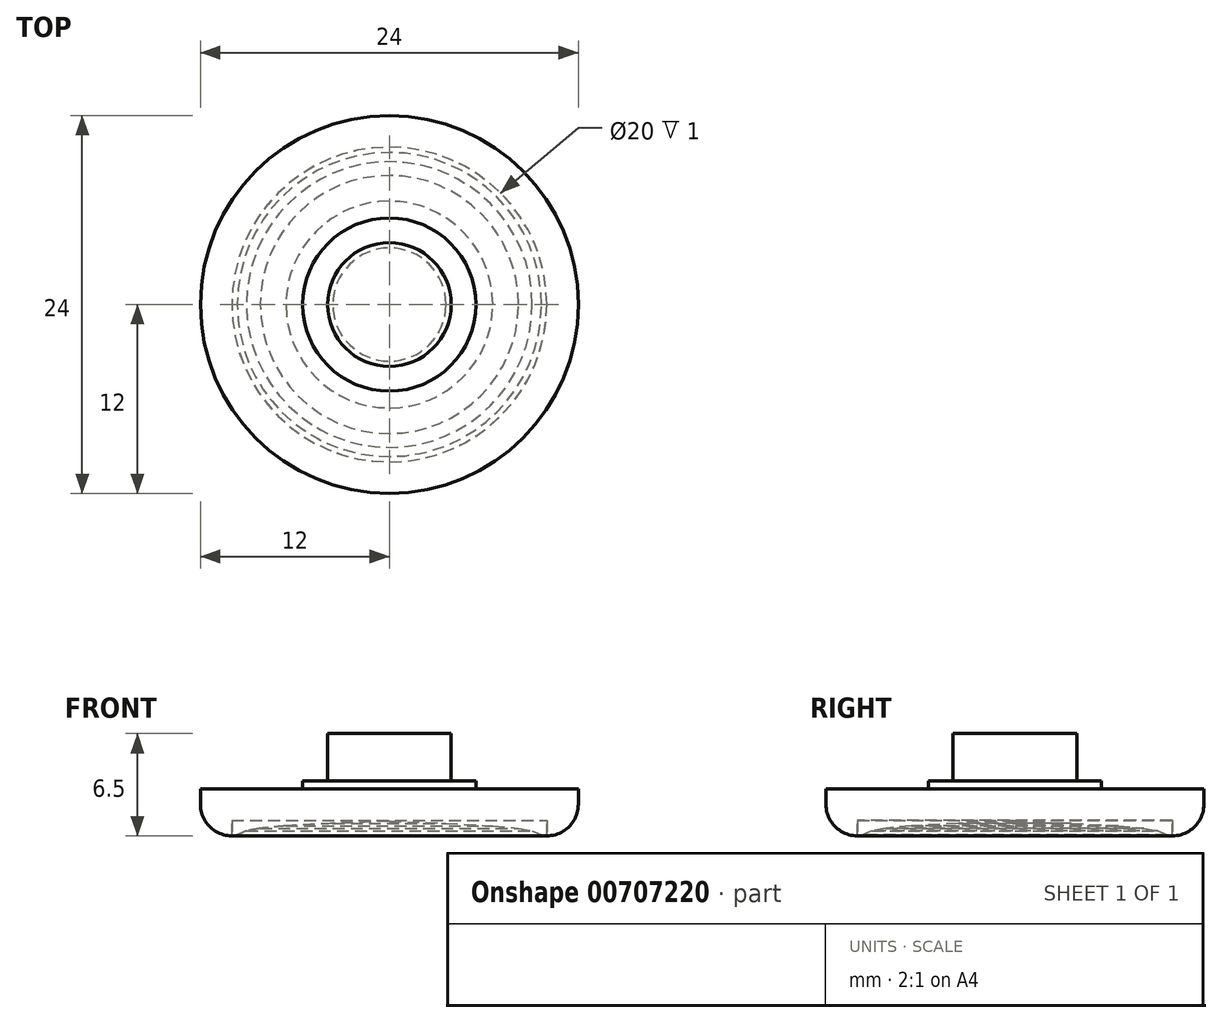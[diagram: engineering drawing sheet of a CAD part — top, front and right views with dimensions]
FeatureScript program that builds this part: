
annotation { "Feature Type Name" : "Feature", "Feature Type Description" : "" }
export const myFeature = defineFeature(function(context is Context, id is Id, definition is map)
    precondition{}
    {
        {
            var Q0;
            Q0=qCreatedBy(makeId("Top.planeOp"),FACE);
            var sketch = newSketch(context, id + "F0", { "sketchPlane" : qUnion([Q0])});
            skCircle(sketch, "E0", {"center": v(0, 0) * mm, "radius": 12 * mm});
            skSolve(sketch);
        }
        {
            var Q0;
            Q0 = qSketchRegion(id + "F0", true);
            extrude(context, id + "F1", {"entities" : qUnion([Q0]), "depth" : 2 * mm, "offsetDistance" : 25 * mm});
        }
        {
            var Q0;
            Q0=makeQuery(id+"F1.opExtrude","CAP_FACE",FACE,{"disambiguationData":[OSD([sQuery(id+"F0.wireOp",EDGE,"E0")])],"isStart":true});
            var sketch = newSketch(context, id + "F2", { "sketchPlane" : qUnion([Q0])});
            skCircle(sketch, "E1", {"center": v(0, 0) * mm, "radius": 10 * mm});
            skSolve(sketch);
        }
        {
            var Q0;
            Q0=makeQuery(id+"F2.imprint","IMPRINT",FACE,{"disambiguationData":[TD([[makeQuery(id+"F2.imprint","IMPRINT",EDGE,{"derivedFrom":sQuery(id+"F2.wireOp",EDGE,"E1")}),-1.0]])]});
            extrude(context, id + "F3", {"entities" : qUnion([Q0]), "operationType" : NewBodyOperationType.ADD, "depth" : 1 * mm, "offsetDistance" : 25 * mm});
        }
        {
            var Q0;
            Q0=makeQuery(id+"F3.opExtrude","CAP_EDGE",EDGE,{"disambiguationData":[OSD([sQuery(id+"F0.wireOp",EDGE,"E0")])],"isStart":false});
            fillet(context, id + "F4", {"entities" : qUnion([Q0]), "radius" : 2 * mm, "tangentPropagation" : true, "allowEdgeOverflow" : false});
        }
        {
            var Q0;
            Q0=makeQuery(id+"F1.opExtrude","CAP_FACE",FACE,{"disambiguationData":[OSD([sQuery(id+"F0.wireOp",EDGE,"E0")])],"isStart":false});
            var sketch = newSketch(context, id + "F5", { "sketchPlane" : qUnion([Q0])});
            skCircle(sketch, "E2", {"center": v(0, 0) * mm, "radius": 5.5 * mm});
            skSolve(sketch);
        }
        {
            var Q0;
            Q0=makeQuery(id+"F5.imprint","IMPRINT",FACE,{"disambiguationData":[TD([[makeQuery(id+"F5.imprint","IMPRINT",EDGE,{"derivedFrom":sQuery(id+"F5.wireOp",EDGE,"E2")}),1.0]])]});
            extrude(context, id + "F6", {"entities" : qUnion([Q0]), "operationType" : NewBodyOperationType.ADD, "depth" : .5 * mm, "offsetDistance" : 25 * mm});
        }
        {
            var Q0;
            Q0=makeQuery(id+"F6.opExtrude","CAP_FACE",FACE,{"disambiguationData":[OSD([sQuery(id+"F5.wireOp",EDGE,"E2")])],"isStart":false});
            var sketch = newSketch(context, id + "F7", { "sketchPlane" : qUnion([Q0])});
            skCircle(sketch, "E3", {"center": v(0, 0) * mm, "radius": 3.92 * mm});
            skSolve(sketch);
        }
        {
            var Q0;
            Q0=makeQuery(id+"F7.imprint","IMPRINT",FACE,{"disambiguationData":[TD([[makeQuery(id+"F7.imprint","IMPRINT",EDGE,{"derivedFrom":sQuery(id+"F7.wireOp",EDGE,"E3")}),1.0]])]});
            extrude(context, id + "F8", {"entities" : qUnion([Q0]), "operationType" : NewBodyOperationType.ADD, "depth" : 3 * mm, "offsetDistance" : 25 * mm});
        }
        {
            var Q0;
            Q0=qCreatedBy(makeId("Front.planeOp"),FACE);
            var sketch = newSketch(context, id + "F9", { "sketchPlane" : qUnion([Q0])});
            skLineSegment(sketch, "E4", {"start": v(-10, -1) * mm, "end": v(-9.66, -0.95) * mm});
            skLineSegment(sketch, "E5", {"start": v(-9.66, -0.95) * mm, "end": v(-9.39, -0.82) * mm});
            skLineSegment(sketch, "E6", {"start": v(-9.39, -0.82) * mm, "end": v(-9.07, -0.68) * mm});
            skLineSegment(sketch, "E7", {"start": v(-9.07, -0.68) * mm, "end": v(-8.2, -0.52) * mm});
            skLineSegment(sketch, "E8", {"start": v(-8.2, -0.52) * mm, "end": v(-6.57, -0.36) * mm});
            skLineSegment(sketch, "E9", {"start": v(-6.57, -0.36) * mm, "end": v(-3.6, -0.2) * mm});
            skLineSegment(sketch, "E10", {"start": v(-3.6, -0.2) * mm, "end": v(0, -0.06) * mm});
            skLineSegment(sketch, "E11", {"start": v(0, -0.06) * mm, "end": v(0, 0) * mm});
            skLineSegment(sketch, "E12", {"start": v(0, 0) * mm, "end": v(-10, 0) * mm});
            skLineSegment(sketch, "E13", {"start": v(-10, 0) * mm, "end": v(-10, -1) * mm});
            skSolve(sketch);
        }
        {
            var Q0;
            Q0=makeQuery(id+"F9.imprint","IMPRINT",FACE,{"disambiguationData":[TD([[makeQuery(id+"F9.imprint","IMPRINT",EDGE,{"derivedFrom":sQuery(id+"F9.wireOp",EDGE,"E4")}),1.0]])]});
            var Q1;
            Q1=sQuery(id+"F9.wireOp",EDGE,"E11");
            revolve(context, id + "F10", {"surfaceOperationType" : NewSurfaceOperationType.NEW, "entities" : qUnion([Q0]), "axis" : qUnion([Q1]), "revolveType" : RevolveType.FULL});
        }
    });
